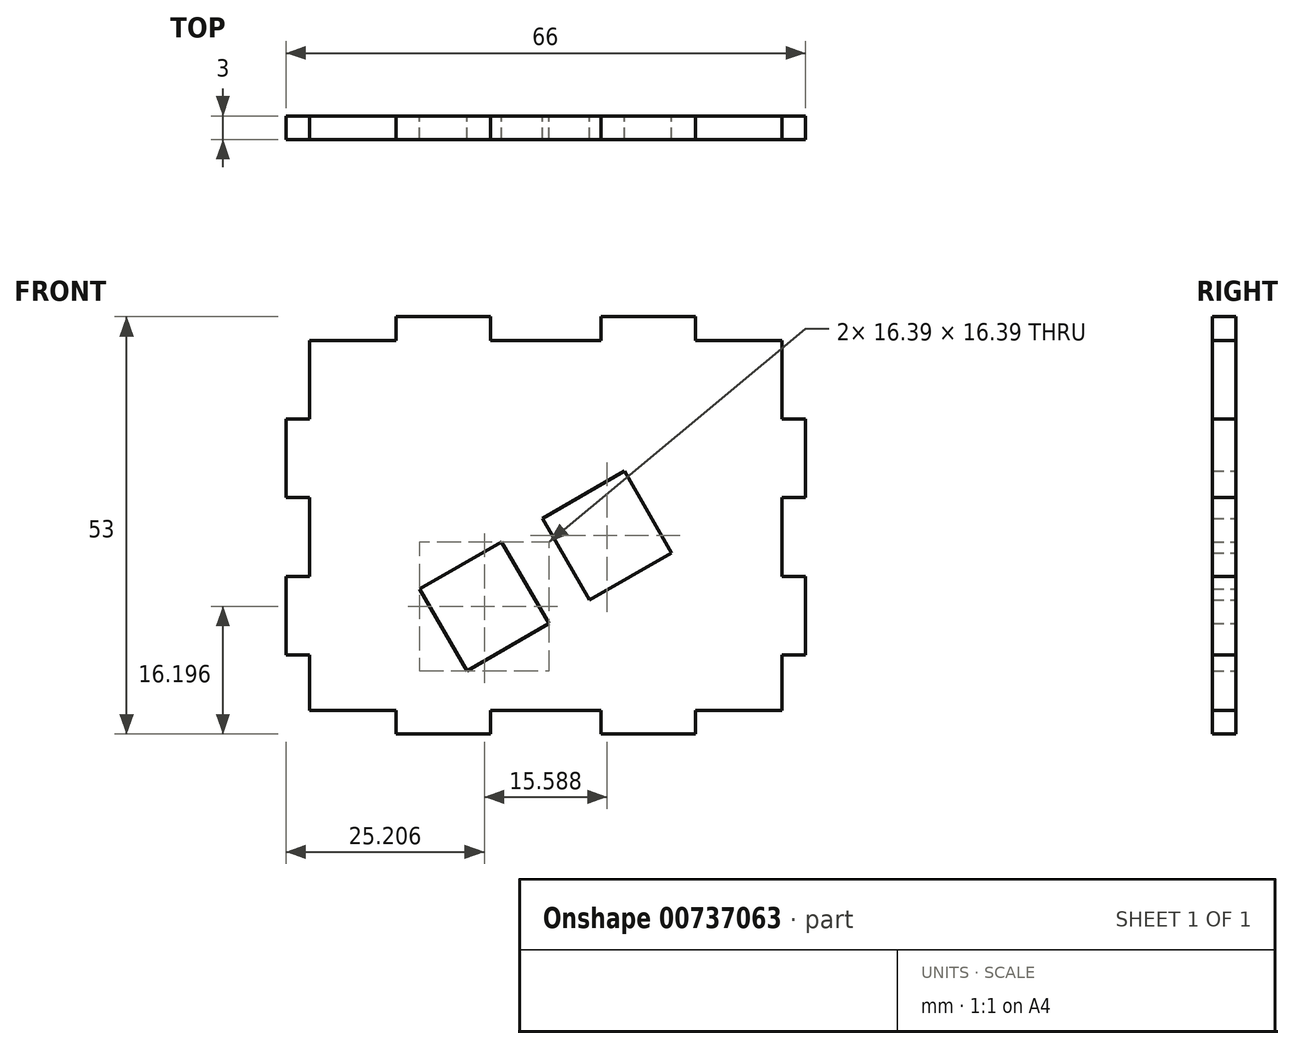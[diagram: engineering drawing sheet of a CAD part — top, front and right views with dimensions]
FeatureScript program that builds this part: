
annotation { "Feature Type Name" : "Feature", "Feature Type Description" : "" }
export const myFeature = defineFeature(function(context is Context, id is Id, definition is map)
    precondition{}
    {
        {
            var Q0;
            Q0=qCreatedBy(makeId("Front.planeOp"),FACE);
            var sketch = newSketch(context, id + "F0", { "sketchPlane" : qUnion([Q0])});
            skLineSegment(sketch, "E0.bottom", {"start": v(33, -26.5) * mm, "end": v(-33, -26.5) * mm, "construction": true});
            skLineSegment(sketch, "E0.top", {"start": v(33, 26.5) * mm, "end": v(-33, 26.5) * mm, "construction": true});
            skLineSegment(sketch, "E0.left", {"start": v(33, -26.5) * mm, "end": v(33, 26.5) * mm, "construction": true});
            skLineSegment(sketch, "E0.right", {"start": v(-33, -26.5) * mm, "end": v(-33, 26.5) * mm, "construction": true});
            skPoint(sketch, "E0.middle", {"position": v(0, 0) * mm});
            skLineSegment(sketch, "E1", {"start": v(-19, 23.5) * mm, "end": v(-19, 26.5) * mm});
            skLineSegment(sketch, "E2", {"start": v(-19, 26.5) * mm, "end": v(-7, 26.5) * mm});
            skLineSegment(sketch, "E3", {"start": v(-7, 26.5) * mm, "end": v(-7, 23.5) * mm});
            skLineSegment(sketch, "E4", {"start": v(-7, 23.5) * mm, "end": v(7, 23.5) * mm});
            skLineSegment(sketch, "E5", {"start": v(7, 23.5) * mm, "end": v(7, 26.5) * mm});
            skLineSegment(sketch, "E6", {"start": v(7, 26.5) * mm, "end": v(19, 26.5) * mm});
            skLineSegment(sketch, "E7", {"start": v(19, 26.5) * mm, "end": v(19, 23.5) * mm});
            skLineSegment(sketch, "E8", {"start": v(19, 23.5) * mm, "end": v(30, 23.5) * mm});
            skLineSegment(sketch, "E9", {"start": v(30, 23.5) * mm, "end": v(30, 13.5) * mm});
            skLineSegment(sketch, "E10", {"start": v(30, 13.5) * mm, "end": v(33, 13.5) * mm});
            skLineSegment(sketch, "E11", {"start": v(33, 13.5) * mm, "end": v(33, 3.5) * mm});
            skLineSegment(sketch, "E12", {"start": v(33, 3.5) * mm, "end": v(30, 3.5) * mm});
            skLineSegment(sketch, "E13", {"start": v(30, 3.5) * mm, "end": v(30, -6.5) * mm});
            skLineSegment(sketch, "E14", {"start": v(30, -6.5) * mm, "end": v(33, -6.5) * mm});
            skLineSegment(sketch, "E15", {"start": v(33, -6.5) * mm, "end": v(33, -16.5) * mm});
            skLineSegment(sketch, "E16", {"start": v(33, -16.5) * mm, "end": v(30, -16.5) * mm});
            skLineSegment(sketch, "E17", {"start": v(30, -16.5) * mm, "end": v(30, -23.5) * mm});
            skLineSegment(sketch, "E18", {"start": v(30, -23.5) * mm, "end": v(19, -23.5) * mm});
            skLineSegment(sketch, "E19", {"start": v(19, -23.5) * mm, "end": v(19, -26.5) * mm});
            skLineSegment(sketch, "E20", {"start": v(19, -26.5) * mm, "end": v(7, -26.5) * mm});
            skLineSegment(sketch, "E21", {"start": v(7, -26.5) * mm, "end": v(7, -23.5) * mm});
            skLineSegment(sketch, "E22", {"start": v(7, -23.5) * mm, "end": v(-7, -23.5) * mm});
            skLineSegment(sketch, "E23", {"start": v(-7, -23.5) * mm, "end": v(-7, -26.5) * mm});
            skLineSegment(sketch, "E24", {"start": v(-7, -26.5) * mm, "end": v(-19, -26.5) * mm});
            skLineSegment(sketch, "E25", {"start": v(-19, -26.5) * mm, "end": v(-19, -23.5) * mm});
            skLineSegment(sketch, "E26", {"start": v(-19, -23.5) * mm, "end": v(-30, -23.5) * mm});
            skLineSegment(sketch, "E27", {"start": v(-30, -23.5) * mm, "end": v(-30, -16.5) * mm});
            skLineSegment(sketch, "E28", {"start": v(-30, -16.5) * mm, "end": v(-33, -16.5) * mm});
            skLineSegment(sketch, "E29", {"start": v(-33, -16.5) * mm, "end": v(-33, -6.5) * mm});
            skLineSegment(sketch, "E30", {"start": v(-33, -6.5) * mm, "end": v(-30, -6.5) * mm});
            skLineSegment(sketch, "E31", {"start": v(-30, -6.5) * mm, "end": v(-30, 3.5) * mm});
            skLineSegment(sketch, "E32", {"start": v(-30, 3.5) * mm, "end": v(-33, 3.5) * mm});
            skLineSegment(sketch, "E33", {"start": v(-33, 3.5) * mm, "end": v(-33, 13.5) * mm});
            skLineSegment(sketch, "E34", {"start": v(-33, 13.5) * mm, "end": v(-30, 13.5) * mm});
            skLineSegment(sketch, "E35", {"start": v(-30, 13.5) * mm, "end": v(-30, 23.5) * mm});
            skLineSegment(sketch, "E36", {"start": v(-30, 23.5) * mm, "end": v(-19, 23.5) * mm});
            skLineSegment(sketch, "E37", {"start": v(-10, -18.5) * mm, "end": v(0.4, -12.5) * mm});
            skLineSegment(sketch, "E38", {"start": v(0.4, -12.5) * mm, "end": v(-5.6, -2.1) * mm});
            skLineSegment(sketch, "E39", {"start": v(-5.6, -2.1) * mm, "end": v(-16, -8.1) * mm});
            skLineSegment(sketch, "E40", {"start": v(-16, -8.1) * mm, "end": v(-10, -18.5) * mm});
            skLineSegment(sketch, "E41", {"start": v(-16, -8.1) * mm, "end": v(10, 6.9) * mm, "construction": true});
            skLineSegment(sketch, "E42", {"start": v(10, 6.9) * mm, "end": v(-0.4, 0.9) * mm});
            skLineSegment(sketch, "E43", {"start": v(-10, -18.5) * mm, "end": v(16, -3.5) * mm, "construction": true});
            skLineSegment(sketch, "E44", {"start": v(-0.4, 0.9) * mm, "end": v(5.6, -9.5) * mm});
            skLineSegment(sketch, "E45", {"start": v(10, 6.9) * mm, "end": v(16, -3.5) * mm});
            skLineSegment(sketch, "E46", {"start": v(16, -3.5) * mm, "end": v(5.6, -9.5) * mm});
            skLineSegment(sketch, "E47", {"start": v(-13, -13.3) * mm, "end": v(13, 1.7) * mm, "construction": true});
            skLineSegment(sketch, "E48", {"start": v(-3, -0.6) * mm, "end": v(3, -11) * mm, "construction": true});
            skPoint(sketch, "E49", {"position": v(0, -5.8) * mm});
            skSolve(sketch);
        }
        {
            var Q0;
            Q0=makeQuery(id+"F0.imprint","IMPRINT",FACE,{"disambiguationData":[TD([[makeQuery(id+"F0.imprint","IMPRINT",EDGE,{"derivedFrom":sQuery(id+"F0.wireOp",EDGE,"B01e6BRD-3qSi-BTNb-VBWV-SjxLaU1JZbyH")}),-1.0]])]});
            var Q1;
            Q1=makeQuery(id+"F0.imprint","IMPRINT",FACE,{"disambiguationData":[TD([[makeQuery(id+"F0.imprint","IMPRINT",EDGE,{"derivedFrom":sQuery(id+"F0.wireOp",EDGE,"E1")}),-1.0]])]});
            extrude(context, id + "F1", {"entities" : qUnion([Q0, Q1]), "depth" : 3 * mm, "offsetDistance" : 25 * mm});
        }
    });
